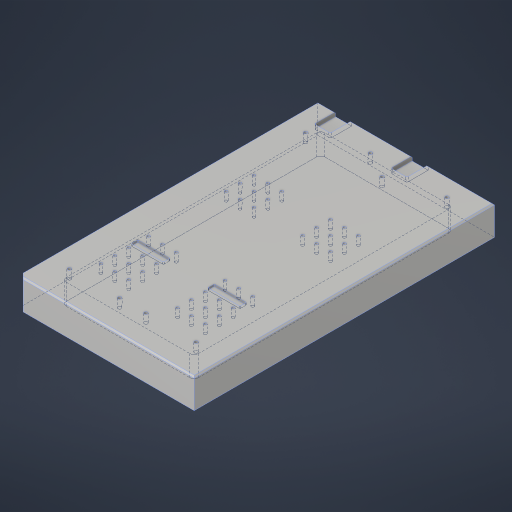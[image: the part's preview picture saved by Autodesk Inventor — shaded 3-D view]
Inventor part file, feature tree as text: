
AUTODESK INVENTOR PART (.ipt)
format: ipt  version: 2024 (Build 280153000, 153)  size: 354,304 bytes
history: native  units: in
note: dims shown in document units (in); Inventor stores cm internally (conversion verified against a paired STEP export)
features: sketch x5, extrude x4, hole x2, chamfer x2
ambient origin geometry x8: Origin, YZ Plane, XZ Plane, XY Plane, X Axis, Y Axis, Z Axis, Center Point
bodies: Solid1 (feature_tree)
feature tree (13):
  extrude  "Extrusion1"  Depth=8.5in
  hole  "Hole2"  [1 undecoded]
  extrude  "Extrusion8"  Depth=6.6844in
  extrude  "Extrusion9"  Depth=0.5906in
  chamfer  "Chamfer2"  Distance=0.0591in
  extrude  "Extrusion10"  Depth=2.374in
  chamfer  "Chamfer4"  Distance=2.5591in
  hole  "Hole3"  [1 undecoded]
  sketch  "Sketch9"  dims[d0=5.0in d1=8.5in]
  sketch  "Sketch10"  dims[d2=0.8323in d3=0.0in d120=0.0394in d121=0.0787in d122=45.0deg]
  sketch  "Sketch11"  dims[d126=1.4213in d127=6.6844in]
  sketch  "Sketch12"  dims[d128=7.0984in d129=0.5906in]
  sketch  "Sketch13"  dims[d130=0.878in d131=0.0984in d132=0.2362in d133=0.1575in d134=0.0787in d135=90.0deg d136=0.315in d137=0.8108in d138=0.0591in d139=0.0in d140=2.374in d141=2.5591in d142=0.8465in d143=0.9094in d144=0.0197in d145=0.5039in d146=0.9567in d147=0.6024in d148=0.128in d149=0.0in d150=0.0394in d151=0.748in d152=0.748in d153=0.1181in d154=0.5906in d155=0.0in d156=0.1575in d157=0.0787in d158=45.0deg d160=0.5118in d161=0.4331in d162=0.7874in d164=2.1654in d165=0.3937in d167=0.3937in d169=0.7874in d171=2.1654in d172=0.3937in d174=0.3937in d176=0.7874in d178=2.1654in d179=0.3937in d181=0.3937in d183=1.1811in d185=0.3937in d186=1.1811in d188=0.3937in d191=0.7874in d193=3.5433in d194=0.7874in d196=2.1654in d199=0.9055in d200=1.4567in d201=0.0787in d202=0.2362in d203=0.1575in d204=0.0787in d205=90.0deg d206=0.315in d207=0.8108in]
note: 2 required parameter values undecoded (feature->parameter linkage not recoverable at this tier; creation-order binding heuristic only, values carry confidence <= 0.55)
